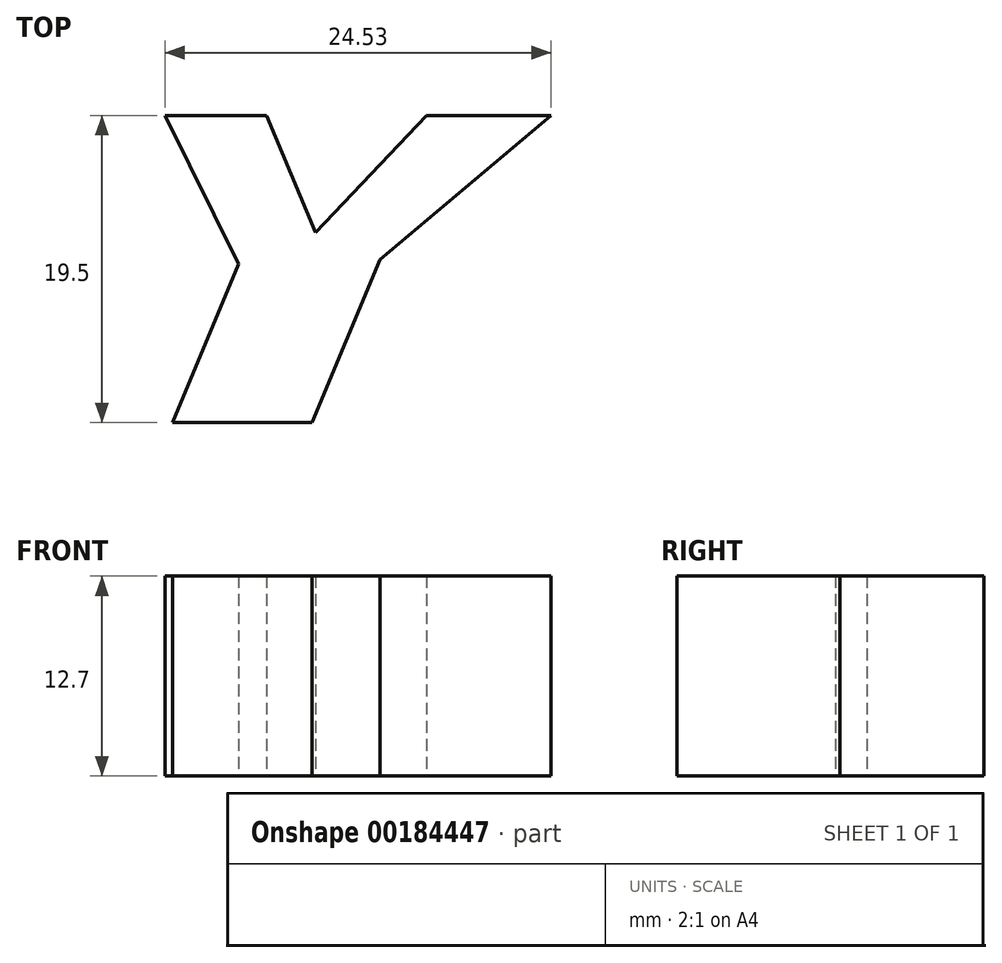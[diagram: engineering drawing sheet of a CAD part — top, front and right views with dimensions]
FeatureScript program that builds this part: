
annotation { "Feature Type Name" : "Feature", "Feature Type Description" : "" }
export const myFeature = defineFeature(function(context is Context, id is Id, definition is map)
    precondition{}
    {
        {
            var Q0;
            Q0=qCreatedBy(makeId("Top.planeOp"),FACE);
            var sketch = newSketch(context, id + "F0", { "sketchPlane" : qUnion([Q0])});
            skLineSegment(sketch, "E0", {"start": v(-2.83, -9.11) * mm, "end": v(1.56, 1.44) * mm});
            skLineSegment(sketch, "E1", {"start": v(1.56, 1.44) * mm, "end": v(-3.38, 11.4) * mm});
            skLineSegment(sketch, "E2", {"start": v(-2.83, -9.11) * mm, "end": v(7.13, -9.11) * mm});
            skLineSegment(sketch, "E3", {"start": v(23.36, 11.4) * mm, "end": v(13.84, 11.4) * mm});
            skLineSegment(sketch, "E4", {"start": v(4.24, 11.4) * mm, "end": v(-3.38, 11.4) * mm});
            skLineSegment(sketch, "E5", {"start": v(23.36, 11.4) * mm, "end": v(11.52, 1.44) * mm});
            skLineSegment(sketch, "E6", {"start": v(11.52, 1.44) * mm, "end": v(7.13, -9.11) * mm});
            skLineSegment(sketch, "E7", {"start": v(7.17, 4.38) * mm, "end": v(13.84, 11.4) * mm});
            skLineSegment(sketch, "E8", {"start": v(4.24, 11.4) * mm, "end": v(7.17, 4.38) * mm});
            skLineSegment(sketch, "E9.0", {"start": v(3.9, 10.9) * mm, "end": v(7, 3.46) * mm});
            skLineSegment(sketch, "E9.1", {"start": v(7, 3.46) * mm, "end": v(14.06, 10.9) * mm});
            skLineSegment(sketch, "E9.2", {"start": v(3.9, 10.9) * mm, "end": v(-2.56, 10.9) * mm});
            skLineSegment(sketch, "E9.3", {"start": v(21.97, 10.9) * mm, "end": v(14.06, 10.9) * mm});
            skLineSegment(sketch, "E9.4", {"start": v(21.97, 10.9) * mm, "end": v(11.1, 1.75) * mm});
            skLineSegment(sketch, "E9.5", {"start": v(2.12, 1.46) * mm, "end": v(-2.56, 10.9) * mm});
            skLineSegment(sketch, "E9.6", {"start": v(-2.06, -8.6) * mm, "end": v(2.12, 1.46) * mm});
            skLineSegment(sketch, "E9.7", {"start": v(-2.06, -8.6) * mm, "end": v(6.79, -8.6) * mm});
            skLineSegment(sketch, "E9.8", {"start": v(11.1, 1.75) * mm, "end": v(6.79, -8.6) * mm});
            skSolve(sketch);
        }
        {
            var Q0;
            Q0=makeQuery(id+"F0.imprint","IMPRINT",FACE,{"disambiguationData":[TD([[makeQuery(id+"F0.imprint","IMPRINT",EDGE,{"derivedFrom":sQuery(id+"F0.wireOp",EDGE,"E9.0")}),-1.0]])]});
            extrude(context, id + "F1", {"entities" : qUnion([Q0]), "depth" : 12.7 * mm});
        }
    });
